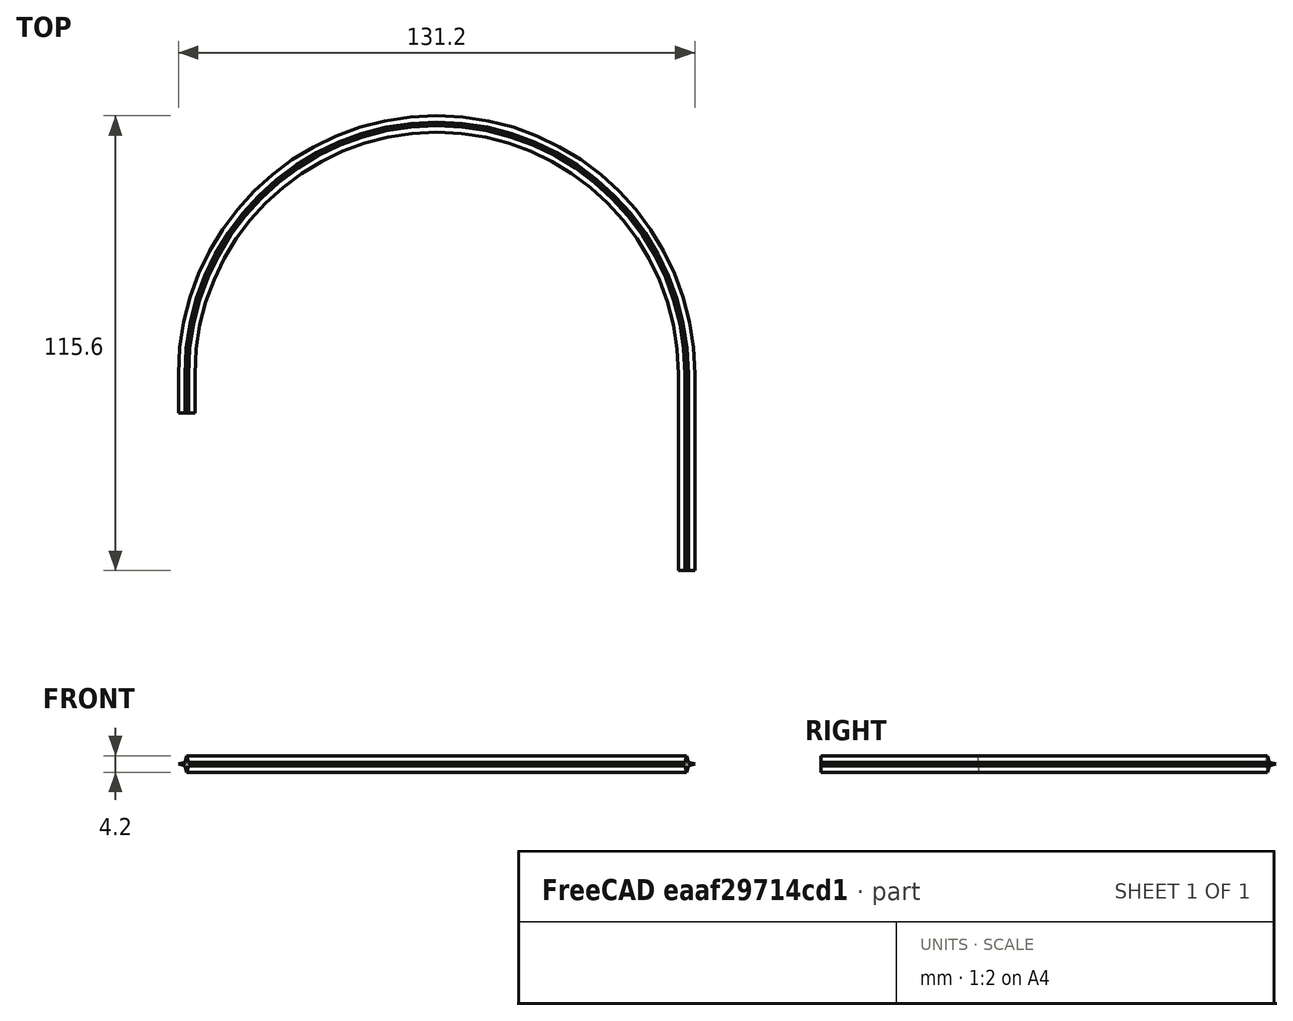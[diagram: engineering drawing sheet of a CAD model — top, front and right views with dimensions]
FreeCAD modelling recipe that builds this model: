
FCSTD DOCUMENT  (FreeCAD 0.19R24344 (Git))
Label: MicroManipulator_Arm_flimsy
Comment: Very thin and flexible arm for MicroManipulator. Too thin for real experiments.
License: Creative Commons Attribution-NonCommercial-ShareAlike
LicenseURL: http://creativecommons.org/licenses/by-nc-sa/4.0/
objects: Sketcher::SketchObject×2, PartDesign::AdditivePipe×1, PartDesign::Body×1
note: 5 computed .brp shape members not serialized (recipe doc carries the construction recipe); baked Part::Feature solids carry a one-line shape summary decoded from their .brp

FEATURE [Sketcher::SketchObject] Sketch
  FullyConstrained = true
  MapMode = 5
  Support = -> [XY_Plane]
  sketch-geometry (3):
    g0: LineSegment StartX=0 StartY=0 StartZ=0 EndX=0 EndY=50 EndZ=0
    g1: LineSegment StartX=-127 StartY=50 StartZ=0 EndX=-127 EndY=40 EndZ=0
    g2: ArcOfCircle CenterX=-63.5 CenterY=50 CenterZ=0 NormalX=0 NormalY=0 NormalZ=1 AngleXU=0 Radius=63.5 StartAngle=0 EndAngle=3.14159
  constraints (8):
    c: Coincident(g0,g-1)
    c: PointOnObject(g0,g-2)
    c: Vertical(g1)
    c: Tangent(g2,g1) = -1.5708
    c: Tangent(g2,g0) = -1.5708
    c: DistanceX(g1,g0) = 127
    c: Distance(g1) = 10
    c: Distance(g0) = 50
FEATURE [Sketcher::SketchObject] Sketch001
  ExternalGeometry = -> [Sketch]
  FullyConstrained = true
  MapMode = 5
  Placement = pos=(0,0,0) rot=(1,0,0;1.5708rad)
  Support = -> [XZ_Plane]
  sketch-geometry (10):
    g0: Circle CenterX=0 CenterY=0 CenterZ=0 NormalX=0 NormalY=0 NormalZ=1 AngleXU=0 Radius=2.1
    g1: LineSegment StartX=2.1 StartY=0 StartZ=0 EndX=0.449013 EndY=0.449013 EndZ=0
    g2: LineSegment StartX=0.449013 StartY=0.449013 StartZ=0 EndX=0 EndY=2.1 EndZ=0
    g3: LineSegment StartX=-2.1 StartY=0 StartZ=0 EndX=-0.449013 EndY=0.449013 EndZ=0
    g4: LineSegment StartX=-0.449013 StartY=0.449013 StartZ=0 EndX=0 EndY=2.1 EndZ=0
    g5: LineSegment StartX=-2.1 StartY=0 StartZ=0 EndX=-0.449013 EndY=-0.449013 EndZ=0
    g6: LineSegment StartX=-0.449013 StartY=-0.449013 StartZ=0 EndX=0 EndY=-2.1 EndZ=0
    g7: LineSegment StartX=2.1 StartY=0 StartZ=0 EndX=0.449013 EndY=-0.449013 EndZ=0
    g8: LineSegment StartX=0.449013 StartY=-0.449013 StartZ=0 EndX=-1e-16 EndY=-2.1 EndZ=0
    g9: LineSegment StartX=-0.449013 StartY=0.449013 StartZ=0 EndX=0.449013 EndY=-0.449013 EndZ=0
  constraints (26):
    c: PointOnObject(g2,g0)
    c: PointOnObject(g3,g0)
    c: PointOnObject(g6,g0)
    c: PointOnObject(g1,g0)
    c: Coincident(g0,g-1)
    c: Distance(g3,g1) = 4.2
    c: PointOnObject(g2,g-2)
    c: Coincident(g2,g1)
    c: Coincident(g4,g3)
    c: Coincident(g4,g2)
    c: Coincident(g5,g3)
    c: Coincident(g6,g5)
    c: Coincident(g7,g1)
    c: Coincident(g8,g7)
    c: Coincident(g8,g6)
    c: Horizontal(g1,g3)
    c: Vertical(g7,g1)
    c: Symmetric(g5,g3,g-1)
    c: Symmetric(g5,g7,g-2)
    c: Distance(g7,g3) = 1.27
    c: Coincident(g9,g3)
    c: Coincident(g9,g7)
    c: Angle(g9) = -0.785398
    c: PointOnObject(g3,g-1)
    c: PointOnObject(g6,g-2)
    c: PointOnObject(g1,g-1)
FEATURE [PartDesign::AdditivePipe] AdditivePipe
  AuxilleryCurvelinear = true
  AuxillerySpineTangent = false
  Binormal = (0,0,0)
  Mode = 0
  Placement = pos=(0,0,0) rot=(1,0,0;1.5708rad)
  Profile = -> Sketch001
  Spine = -> Sketch
  SpineTangent = false
  Transformation = 0
  Transition = 0
FEATURE [PartDesign::Body] Body  label="Arm_flimsy"
  Group = -> [Sketch,Sketch001,AdditivePipe]
  Origin = -> Origin
  Tip = -> AdditivePipe
